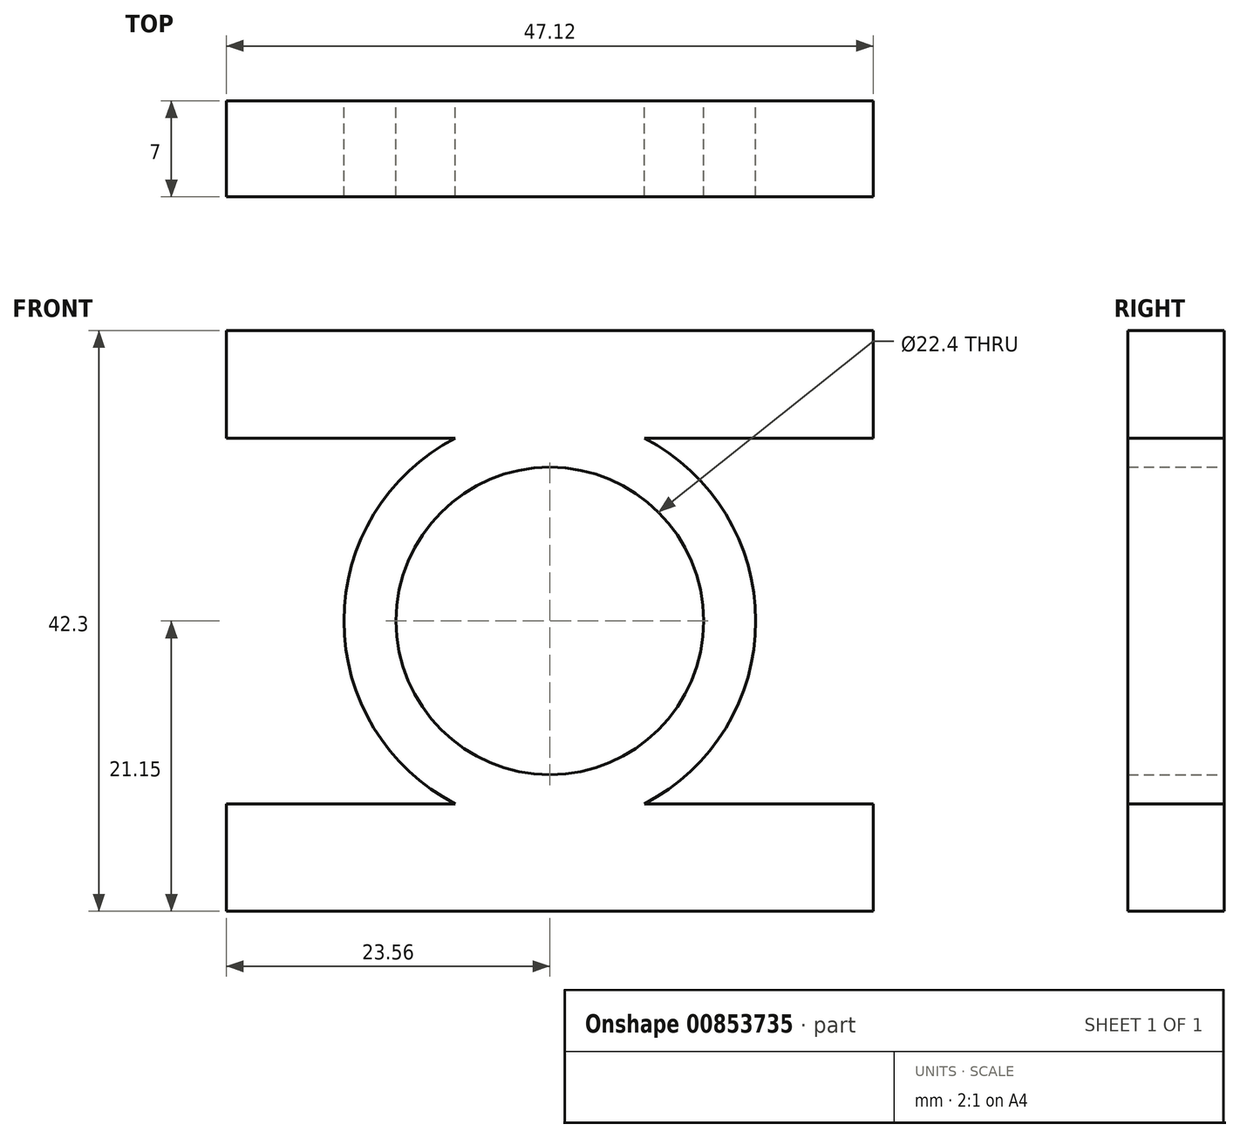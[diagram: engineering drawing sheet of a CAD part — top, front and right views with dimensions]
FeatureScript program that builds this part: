
annotation { "Feature Type Name" : "Feature", "Feature Type Description" : "" }
export const myFeature = defineFeature(function(context is Context, id is Id, definition is map)
    precondition{}
    {
        {
            var Q0;
            Q0=qCreatedBy(makeId("Front.planeOp"),FACE);
            var sketch = newSketch(context, id + "F0", { "sketchPlane" : qUnion([Q0])});
            skCircle(sketch, "E0", {"center": v(0, 0) * mm, "radius": 11.2 * mm});
            skArc(sketch, "E1", {"start": v(-6.9, 13.32) * mm, "mid": v(-15, 0) * mm, "end": v(-6.9, -13.32) * mm});
            skLineSegment(sketch, "E2", {"start": v(-6.9, -13.32) * mm, "end": v(-23.56, -13.32) * mm});
            skLineSegment(sketch, "E3", {"start": v(-23.56, -13.32) * mm, "end": v(-23.56, -21.15) * mm});
            skLineSegment(sketch, "E4", {"start": v(-23.56, -21.15) * mm, "end": v(0, -21.15) * mm});
            skLineSegment(sketch, "E5.MirrorCS", {"start": v(23.56, -21.15) * mm, "end": v(0, -21.15) * mm});
            skLineSegment(sketch, "E6.MirrorCS", {"start": v(23.56, -13.32) * mm, "end": v(23.56, -21.15) * mm});
            skLineSegment(sketch, "E7.MirrorCS", {"start": v(6.9, -13.32) * mm, "end": v(23.56, -13.32) * mm});
            skLineSegment(sketch, "E8.MirrorCS", {"start": v(6.9, 13.32) * mm, "end": v(23.56, 13.32) * mm});
            skLineSegment(sketch, "E9.MirrorCS", {"start": v(23.56, 13.32) * mm, "end": v(23.56, 21.15) * mm});
            skLineSegment(sketch, "E10.MirrorCS", {"start": v(23.56, 21.15) * mm, "end": v(0, 21.15) * mm});
            skLineSegment(sketch, "E11.MirrorCS", {"start": v(-23.56, 21.15) * mm, "end": v(0, 21.15) * mm});
            skLineSegment(sketch, "E12.MirrorCS", {"start": v(-6.9, 13.32) * mm, "end": v(-23.56, 13.32) * mm});
            skLineSegment(sketch, "E13.MirrorCS", {"start": v(-23.56, 13.32) * mm, "end": v(-23.56, 21.15) * mm});
            skArc(sketch, "E14.trimOffspring", {"start": v(6.9, -13.32) * mm, "mid": v(15, 0) * mm, "end": v(6.9, 13.32) * mm});
            skPoint(sketch, "E15.orphan", {"position": v(0, -13.32) * mm});
            skPoint(sketch, "E16.orphan", {"position": v(0, 13.32) * mm});
            skSolve(sketch);
        }
        {
            var Q0;
            Q0=makeQuery(id+"F0.imprint","IMPRINT",FACE,{"disambiguationData":[TD([[makeQuery(id+"F0.imprint","IMPRINT",EDGE,{"derivedFrom":sQuery(id+"F0.wireOp",EDGE,"E0")}),-1.0]])]});
            var Q1;
            Q1=makeQuery(id+"F0.imprint","IMPRINT",FACE,{"disambiguationData":[TD([[makeQuery(id+"F0.imprint","IMPRINT",EDGE,{"derivedFrom":sQuery(id+"F0.wireOp",EDGE,"896162b2-5c40-4931-a0e0-0c6b43d615730.MirrorCS")}),1.0]])]});
            var Q2;
            Q2=makeQuery(id+"F0.imprint","IMPRINT",FACE,{"disambiguationData":[TD([[makeQuery(id+"F0.imprint","IMPRINT",EDGE,{"derivedFrom":sQuery(id+"F0.wireOp",EDGE,"zCWfAizq-xyLL-SQmk-lap8-J1BiGs4OgDpY")}),-1.0]])]});
            extrude(context, id + "F1", {"entities" : qUnion([Q0, Q1, Q2]), "depth" : 7 * mm, "offsetDistance" : 25 * mm});
        }
    });
